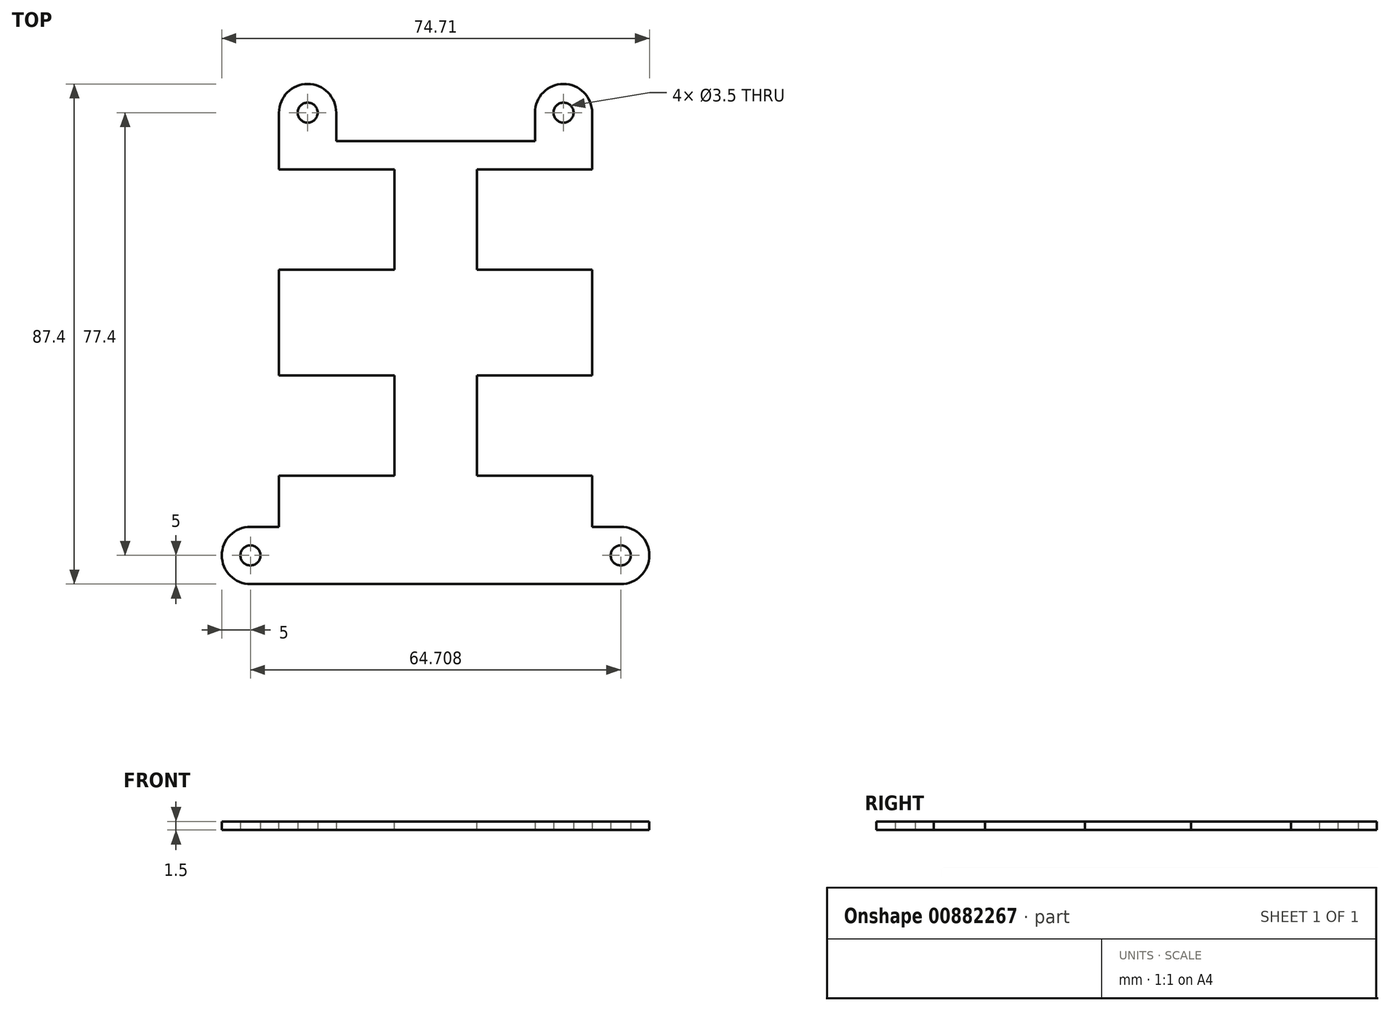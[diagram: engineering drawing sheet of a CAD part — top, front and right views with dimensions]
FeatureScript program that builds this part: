
annotation { "Feature Type Name" : "Feature", "Feature Type Description" : "" }
export const myFeature = defineFeature(function(context is Context, id is Id, definition is map)
    precondition{}
    {
        {
            var Q0;
            Q0=qCreatedBy(makeId("Top.planeOp"),FACE);
            var sketch = newSketch(context, id + "F0", { "sketchPlane" : qUnion([Q0])});
            skLineSegment(sketch, "E0.bottom", {"start": v(0, 0) * mm, "end": v(51.3, 0) * mm});
            skLineSegment(sketch, "E0.top", {"start": v(0, 74) * mm, "end": v(51.3, 74) * mm});
            skLineSegment(sketch, "E0.left", {"start": v(0, 0) * mm, "end": v(0, 74) * mm});
            skLineSegment(sketch, "E0.right", {"start": v(51.3, 0) * mm, "end": v(51.3, 74) * mm});
            skLineSegment(sketch, "E1.bottom", {"start": v(0, 69) * mm, "end": v(16.7, 69) * mm, "construction": true});
            skLineSegment(sketch, "E1.top", {"start": v(0, 55) * mm, "end": v(16.7, 55) * mm, "construction": true});
            skLineSegment(sketch, "E1.left", {"start": v(0, 69) * mm, "end": v(0, 55) * mm, "construction": true});
            skLineSegment(sketch, "E1.right", {"start": v(16.7, 69) * mm, "end": v(16.7, 55) * mm, "construction": true});
            skLineSegment(sketch, "E2.bottom", {"start": v(0, 33) * mm, "end": v(16.7, 33) * mm, "construction": true});
            skLineSegment(sketch, "E2.top", {"start": v(0, 19) * mm, "end": v(16.7, 19) * mm, "construction": true});
            skLineSegment(sketch, "E2.left", {"start": v(0, 33) * mm, "end": v(0, 19) * mm, "construction": true});
            skLineSegment(sketch, "E2.right", {"start": v(16.7, 33) * mm, "end": v(16.7, 19) * mm, "construction": true});
            skLineSegment(sketch, "E3.bottom", {"start": v(51.3, 69) * mm, "end": v(34.6, 69) * mm, "construction": true});
            skLineSegment(sketch, "E3.top", {"start": v(51.3, 55) * mm, "end": v(34.6, 55) * mm, "construction": true});
            skLineSegment(sketch, "E3.left", {"start": v(51.3, 69) * mm, "end": v(51.3, 55) * mm, "construction": true});
            skLineSegment(sketch, "E3.right", {"start": v(34.6, 69) * mm, "end": v(34.6, 55) * mm, "construction": true});
            skLineSegment(sketch, "E4.bottom", {"start": v(51.3, 33) * mm, "end": v(34.6, 33) * mm, "construction": true});
            skLineSegment(sketch, "E4.top", {"start": v(51.3, 19) * mm, "end": v(34.6, 19) * mm, "construction": true});
            skLineSegment(sketch, "E4.left", {"start": v(51.3, 33) * mm, "end": v(51.3, 19) * mm, "construction": true});
            skLineSegment(sketch, "E4.right", {"start": v(34.6, 33) * mm, "end": v(34.6, 19) * mm, "construction": true});
            skCircle(sketch, "E5", {"center": v(11.21, 3.92) * mm, "radius": 1.6 * mm});
            skCircle(sketch, "E6", {"center": v(32.51, 3.92) * mm, "radius": 1.6 * mm});
            skCircle(sketch, "E7", {"center": v(49.43, 3.92) * mm, "radius": 1.6 * mm});
            skCircle(sketch, "E8", {"center": v(49.43, 72.12) * mm, "radius": 1.6 * mm});
            skCircle(sketch, "E9", {"center": v(1.88, 72.12) * mm, "radius": 1.6 * mm});
            skLineSegment(sketch, "E10", {"start": v(1.88, 72.12) * mm, "end": v(49.43, 72.12) * mm, "construction": true});
            skSolve(sketch);
        }
        {
            var Q0;
            {var subQ10=sQuery(id+"F0.wireOp",EDGE,"E0.bottom");Q0=makeQuery(id+"F0.imprint","IMPRINT",FACE,{"disambiguationData":[TD([[makeQuery(id+"F0.imprint","IMPRINT",EDGE,{"derivedFrom":subQ10}),1.0]])]});}
            var sketch = newSketch(context, id + "F1", { "sketchPlane" : qUnion([Q0])});
            skLineSegment(sketch, "E11.0", {"start": v(-1.7, -1.7) * mm, "end": v(-1.7, 75.7) * mm});
            skLineSegment(sketch, "E11.1", {"start": v(-1.7, -1.7) * mm, "end": v(53, -1.7) * mm});
            skLineSegment(sketch, "E11.2", {"start": v(53, -1.7) * mm, "end": v(53, 75.7) * mm});
            skLineSegment(sketch, "E11.3", {"start": v(-1.7, 75.7) * mm, "end": v(53, 75.7) * mm});
            skSolve(sketch);
        }
        {
            var Q0;
            Q0=qSketchRegion(id+"F1",true);
            extrude(context, id + "F2", {"entities" : qUnion([Q0]), "depth" : 1.5 * mm, "offsetDistance" : 25 * mm});
        }
        {
            var Q0;
            Q0=makeQuery(id+"F2.opExtrude","CAP_FACE",FACE,{"disambiguationData":[OSD([sQuery(id+"F1.wireOp",EDGE,"E11.0"),sQuery(id+"F1.wireOp",EDGE,"E11.1"),sQuery(id+"F1.wireOp",EDGE,"E11.2"),sQuery(id+"F1.wireOp",EDGE,"E11.3")])],"isStart":true});
            var sketch = newSketch(context, id + "F3", { "sketchPlane" : qUnion([Q0])});
            skArc(sketch, "E12", {"start": v(-6.7, 1.7) * mm, "mid": v(-11.7, -3.3) * mm, "end": v(-6.7, -8.3) * mm});
            skArc(sketch, "E13", {"start": v(-1.7, -80.7) * mm, "mid": v(3.3, -85.7) * mm, "end": v(8.3, -80.7) * mm});
            skLineSegment(sketch, "E14", {"start": v(-1.7, 1.7) * mm, "end": v(-6.7, 1.7) * mm});
            skLineSegment(sketch, "E15", {"start": v(-6.7, -8.3) * mm, "end": v(-1.7, -8.3) * mm});
            skLineSegment(sketch, "E16", {"start": v(25.65, 1.7) * mm, "end": v(25.65, -75.7) * mm, "construction": true});
            skLineSegment(sketch, "E17", {"start": v(-1.7, 1.7) * mm, "end": v(-1.7, -8.3) * mm});
            skLineSegment(sketch, "E18", {"start": v(-1.7, -75.7) * mm, "end": v(-1.7, -80.7) * mm});
            skLineSegment(sketch, "E19", {"start": v(8.3, -80.7) * mm, "end": v(8.3, -75.7) * mm});
            skLineSegment(sketch, "E20", {"start": v(-1.7, -75.7) * mm, "end": v(8.3, -75.7) * mm});
            skLineSegment(sketch, "E21.MirrorCS", {"start": v(58, -8.3) * mm, "end": v(53, -8.3) * mm});
            skLineSegment(sketch, "E22.MirrorCS", {"start": v(43, -80.7) * mm, "end": v(43, -75.7) * mm});
            skLineSegment(sketch, "E23.MirrorCS", {"start": v(53, 1.7) * mm, "end": v(58, 1.7) * mm});
            skLineSegment(sketch, "E24.MirrorCS", {"start": v(53, -75.7) * mm, "end": v(53, -80.7) * mm});
            skLineSegment(sketch, "E25.MirrorCS", {"start": v(53, 1.7) * mm, "end": v(53, -8.3) * mm});
            skLineSegment(sketch, "E26.MirrorCS", {"start": v(53, -75.7) * mm, "end": v(43, -75.7) * mm});
            skArc(sketch, "E27.MirrorCS", {"start": v(53, -80.7) * mm, "mid": v(48, -85.7) * mm, "end": v(43, -80.7) * mm});
            skArc(sketch, "E28.MirrorCS", {"start": v(58, 1.7) * mm, "mid": v(63, -3.3) * mm, "end": v(58, -8.3) * mm});
            skCircle(sketch, "E29", {"center": v(-6.7, -3.3) * mm, "radius": 1.75 * mm});
            skCircle(sketch, "E30", {"center": v(58, -3.3) * mm, "radius": 1.75 * mm});
            skCircle(sketch, "E31", {"center": v(48, -80.7) * mm, "radius": 1.75 * mm});
            skCircle(sketch, "E32", {"center": v(3.3, -80.7) * mm, "radius": 1.75 * mm});
            skSolve(sketch);
        }
        {
            var Q0;
            Q0=qSketchRegion(id+"F3",true);
            var Q1;
            {var subQ0=sQuery(id+"F1.wireOp",EDGE,"E11.0");var subQ1=sQuery(id+"F1.wireOp",EDGE,"E11.2");var subQ2=sQuery(id+"F1.wireOp",EDGE,"E11.3");Q1=makeQuery(id+"FCauK0S3PUZOb4y_1.boolean.opBoolean","SPLIT",FACE,{"disambiguationData":[TD([makeQuery(id+"F2.opExtrude","SWEPT_FACE",FACE,{"disambiguationData":[OSD([subQ2])]})])],"derivedFrom":makeQuery(id+"F2.opExtrude","CAP_FACE",FACE,{"disambiguationData":[OSD([subQ0,sQuery(id+"F1.wireOp",EDGE,"E11.1"),subQ1,subQ2])],"isStart":false})});}
            extrude(context, id + "F4", {"entities" : qUnion([Q0]), "operationType" : NewBodyOperationType.ADD, "oppositeDirection" : true, "depth" : 1.5 * mm, "endBoundEntityFace" : qUnion([Q1]), "offsetDistance" : 25 * mm});
        }
        {
            var Q0;
            Q0=makeQuery(id+"F4.boolean.opBoolean","MERGE",FACE,{"derivedFrom":[makeQuery(id+"F2.opExtrude","CAP_FACE",FACE,{"disambiguationData":[OSD([sQuery(id+"F1.wireOp",EDGE,"E11.0"),sQuery(id+"F1.wireOp",EDGE,"E11.1"),sQuery(id+"F1.wireOp",EDGE,"E11.2"),sQuery(id+"F1.wireOp",EDGE,"E11.3")])],"isStart":false}),makeQuery(id+"F4.opExtrude","CAP_FACE",FACE,{"disambiguationData":[OSD([sQuery(id+"F3.wireOp",EDGE,"E12"),sQuery(id+"F3.wireOp",EDGE,"E14"),sQuery(id+"F3.wireOp",EDGE,"E15"),sQuery(id+"F3.wireOp",EDGE,"E17"),sQuery(id+"F3.wireOp",EDGE,"E29")])],"isStart":false}),makeQuery(id+"F4.opExtrude","CAP_FACE",FACE,{"disambiguationData":[OSD([sQuery(id+"F3.wireOp",EDGE,"E13"),sQuery(id+"F3.wireOp",EDGE,"E18"),sQuery(id+"F3.wireOp",EDGE,"E19"),sQuery(id+"F3.wireOp",EDGE,"E20"),sQuery(id+"F3.wireOp",EDGE,"E32")])],"isStart":false}),makeQuery(id+"F4.opExtrude","CAP_FACE",FACE,{"disambiguationData":[OSD([sQuery(id+"F3.wireOp",EDGE,"E21.MirrorCS"),sQuery(id+"F3.wireOp",EDGE,"E23.MirrorCS"),sQuery(id+"F3.wireOp",EDGE,"E25.MirrorCS"),sQuery(id+"F3.wireOp",EDGE,"E28.MirrorCS"),sQuery(id+"F3.wireOp",EDGE,"E30")])],"isStart":false}),makeQuery(id+"F4.opExtrude","CAP_FACE",FACE,{"disambiguationData":[OSD([sQuery(id+"F3.wireOp",EDGE,"E22.MirrorCS"),sQuery(id+"F3.wireOp",EDGE,"E24.MirrorCS"),sQuery(id+"F3.wireOp",EDGE,"E26.MirrorCS"),sQuery(id+"F3.wireOp",EDGE,"E27.MirrorCS"),sQuery(id+"F3.wireOp",EDGE,"E31")])],"isStart":false})]});
            var sketch = newSketch(context, id + "F5", { "sketchPlane" : qUnion([Q0])});
            skLineSegment(sketch, "E33.0", {"start": v(-1.75, 17.25) * mm, "end": v(18.45, 17.25) * mm});
            skLineSegment(sketch, "E33.1", {"start": v(-1.75, 34.75) * mm, "end": v(-1.75, 17.25) * mm});
            skLineSegment(sketch, "E33.2", {"start": v(-1.75, 34.75) * mm, "end": v(18.45, 34.75) * mm});
            skLineSegment(sketch, "E33.3", {"start": v(18.45, 34.75) * mm, "end": v(18.45, 17.25) * mm});
            skLineSegment(sketch, "E34.0", {"start": v(32.86, 34.75) * mm, "end": v(32.86, 17.25) * mm});
            skLineSegment(sketch, "E34.1", {"start": v(53.06, 34.75) * mm, "end": v(32.86, 34.75) * mm});
            skLineSegment(sketch, "E34.2", {"start": v(53.06, 34.75) * mm, "end": v(53.06, 17.25) * mm});
            skLineSegment(sketch, "E34.3", {"start": v(53.06, 17.25) * mm, "end": v(32.86, 17.25) * mm});
            skLineSegment(sketch, "E35.0", {"start": v(-1.75, 70.75) * mm, "end": v(18.45, 70.75) * mm});
            skLineSegment(sketch, "E35.1", {"start": v(-1.75, 70.75) * mm, "end": v(-1.75, 53.25) * mm});
            skLineSegment(sketch, "E35.2", {"start": v(-1.75, 53.25) * mm, "end": v(18.45, 53.25) * mm});
            skLineSegment(sketch, "E35.3", {"start": v(18.45, 70.75) * mm, "end": v(18.45, 53.25) * mm});
            skLineSegment(sketch, "E36.0", {"start": v(32.86, 70.75) * mm, "end": v(32.86, 53.25) * mm});
            skLineSegment(sketch, "E36.1", {"start": v(53.06, 70.75) * mm, "end": v(32.86, 70.75) * mm});
            skLineSegment(sketch, "E36.2", {"start": v(53.06, 70.75) * mm, "end": v(53.06, 53.25) * mm});
            skLineSegment(sketch, "E36.3", {"start": v(53.06, 53.25) * mm, "end": v(32.86, 53.25) * mm});
            skSolve(sketch);
        }
        {
            var Q0;
            Q0=qSketchRegion(id+"F5",true);
            extrude(context, id + "F6", {"entities" : qUnion([Q0]), "operationType" : NewBodyOperationType.REMOVE, "endBound" : BoundingType.THROUGH_ALL, "oppositeDirection" : true, "depth" : 25 * mm, "offsetDistance" : 25 * mm});
        }
    });
